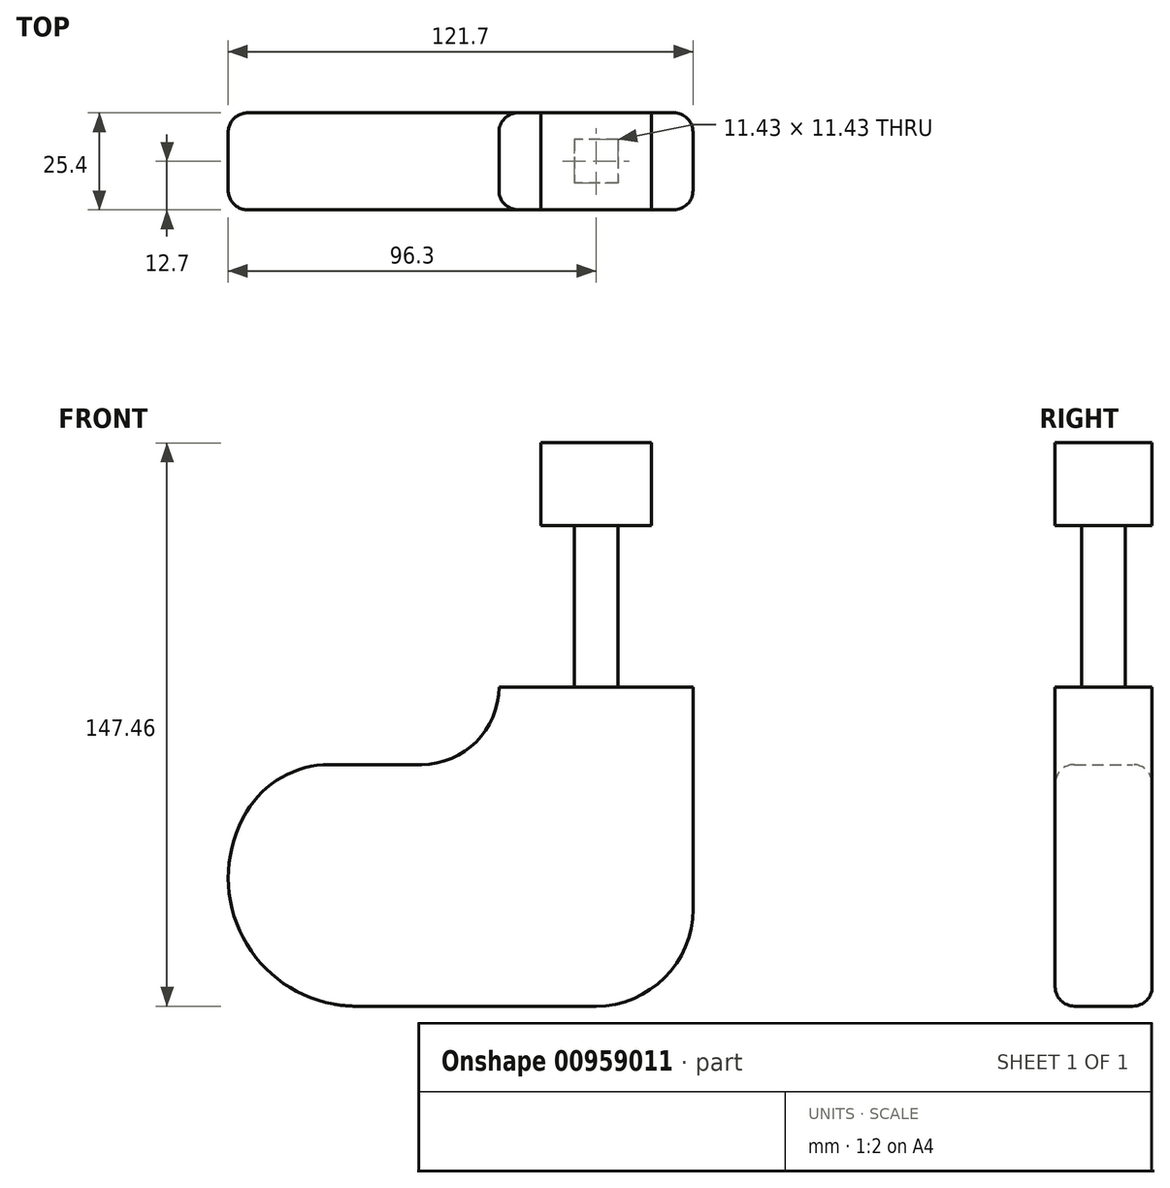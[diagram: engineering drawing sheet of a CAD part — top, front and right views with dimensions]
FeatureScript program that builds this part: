
annotation { "Feature Type Name" : "Feature", "Feature Type Description" : "" }
export const myFeature = defineFeature(function(context is Context, id is Id, definition is map)
    precondition{}
    {
        {
            var Q0;
            Q0=qCreatedBy(makeId("Front.planeOp"),FACE);
            var sketch = newSketch(context, id + "F0", { "sketchPlane" : qUnion([Q0])});
            skLineSegment(sketch, "E0.top", {"start": v(0, -63.5) * mm, "end": v(-25.4, -63.5) * mm});
            skLineSegment(sketch, "E0.left", {"start": v(25.4, 20.06) * mm, "end": v(25.4, -38.1) * mm});
            skPoint(sketch, "E0.middle", {"position": v(0, 0) * mm});
            skLineSegment(sketch, "E1.bottom", {"start": v(-25.4, -63.5) * mm, "end": v(-62.78, -63.5) * mm});
            skLineSegment(sketch, "E1.top", {"start": v(-45.72, -0.26) * mm, "end": v(-69.73, -0.26) * mm});
            skArc(sketch, "E2", {"start": v(-91.55, -12.64) * mm, "mid": v(-93.32, -43.72) * mm, "end": v(-68.83, -62.94) * mm});
            skPoint(sketch, "E3.visualSharp", {"position": v(-25.4, -0.26) * mm});
            skArc(sketch, "E3.filletArc", {"start": v(-45.72, -0.26) * mm, "mid": v(-31.35, 5.7) * mm, "end": v(-25.4, 20.06) * mm});
            skPoint(sketch, "E4.visualSharp", {"position": v(-78.6, -0.26) * mm});
            skArc(sketch, "E4.filletArc", {"start": v(-69.73, -0.26) * mm, "mid": v(-82.28, -3.57) * mm, "end": v(-91.55, -12.64) * mm});
            skPoint(sketch, "E5.visualSharp", {"position": v(-63.5, -63.5) * mm});
            skArc(sketch, "E5.filletArc", {"start": v(-68.83, -62.94) * mm, "mid": v(-65.81, -63.36) * mm, "end": v(-62.78, -63.5) * mm});
            skPoint(sketch, "E6.visualSharp", {"position": v(25.4, -63.5) * mm});
            skArc(sketch, "E6.filletArc", {"start": v(0, -63.5) * mm, "mid": v(17.96, -56.06) * mm, "end": v(25.4, -38.1) * mm});
            skLineSegment(sketch, "E7", {"start": v(-25.4, 20.06) * mm, "end": v(25.4, 20.06) * mm});
            skPoint(sketch, "E0.bottom.start.orphan", {"position": v(25.4, 63.5) * mm});
            skPoint(sketch, "E0.right.start.orphan", {"position": v(-25.4, 63.5) * mm});
            skSolve(sketch);
        }
        {
            var Q0;
            Q0 = qSketchRegion(id + "F0", true);
            extrude(context, id + "F1", {"entities" : qUnion([Q0]), "depth" : 25.4 * mm, "offsetDistance" : 25.4 * mm});
        }
        {
            var Q0;
            Q0=makeQuery(id+"F1.opExtrude","CAP_EDGE",EDGE,{"disambiguationData":[OSD([sQuery(id+"F0.wireOp",EDGE,"E2")])],"isStart":false});
            var Q1;
            Q1=makeQuery(id+"F1.opExtrude","CAP_EDGE",EDGE,{"disambiguationData":[OSD([sQuery(id+"F0.wireOp",EDGE,"E2")])],"isStart":true});
            fillet(context, id + "F2", {"entities" : qUnion([Q0, Q1]), "radius" : 5.08 * mm, "tangentPropagation" : true, "allowEdgeOverflow" : false});
        }
        {
            var Q0;
            Q0=makeQuery(id+"F1.opExtrude","SWEPT_FACE",FACE,{"disambiguationData":[OSD([sQuery(id+"F0.wireOp",EDGE,"E7")])]});
            var sketch = newSketch(context, id + "F3", { "sketchPlane" : qUnion([Q0])});
            skLineSegment(sketch, "E8.bottom", {"start": v(5.72, -6.99) * mm, "end": v(-5.72, -6.99) * mm});
            skLineSegment(sketch, "E8.top", {"start": v(5.72, -18.42) * mm, "end": v(-5.72, -18.42) * mm});
            skLineSegment(sketch, "E8.left", {"start": v(5.72, -6.99) * mm, "end": v(5.72, -18.42) * mm});
            skLineSegment(sketch, "E8.right", {"start": v(-5.72, -6.99) * mm, "end": v(-5.72, -18.42) * mm});
            skPoint(sketch, "E8.middle", {"position": v(0, -12.7) * mm});
            skPoint(sketch, "E8.middle.positionSnap0", {"position": v(25.4, -12.7) * mm});
            skPoint(sketch, "E8.centerSnap0", {"position": v(25.4, -12.7) * mm});
            skSolve(sketch);
        }
        {
            var Q0;
            Q0 = qSketchRegion(id + "F3", true);
            extrude(context, id + "F4", {"entities" : qUnion([Q0]), "operationType" : NewBodyOperationType.ADD, "depth" : 50.8 * mm, "offsetDistance" : 25.4 * mm});
        }
        {
            var Q0;
            Q0=makeQuery(id+"F1.opExtrude","CAP_FACE",FACE,{"disambiguationData":[OSD([sQuery(id+"F0.wireOp",EDGE,"E0.top"),sQuery(id+"F0.wireOp",EDGE,"E0.left"),sQuery(id+"F0.wireOp",EDGE,"E1.bottom"),sQuery(id+"F0.wireOp",EDGE,"E1.top"),sQuery(id+"F0.wireOp",EDGE,"E2"),sQuery(id+"F0.wireOp",EDGE,"E3.filletArc"),sQuery(id+"F0.wireOp",EDGE,"E4.filletArc"),sQuery(id+"F0.wireOp",EDGE,"E5.filletArc"),sQuery(id+"F0.wireOp",EDGE,"E6.filletArc"),sQuery(id+"F0.wireOp",EDGE,"E7")])],"isStart":false});
            cPlane(context, id + "F5", {"entities" : qUnion([Q0]), "cplaneType" : CPlaneType.OFFSET, "offset" : 0 * mm, "width" : 152.4 * mm, "height" : 152.4 * mm});
        }
        {
            var Q0;
            Q0=qCreatedBy(id+"F5.planeOp",FACE);
            var sketch = newSketch(context, id + "F6", { "sketchPlane" : qUnion([Q0])});
            skLineSegment(sketch, "E9.left", {"start": v(14.46, 83.96) * mm, "end": v(14.46, 71.1) * mm});
            skLineSegment(sketch, "E9.right", {"start": v(-14.46, 83.96) * mm, "end": v(-14.46, 71.1) * mm});
            skPoint(sketch, "E9.middle", {"position": v(0, 71.1) * mm});
            skPoint(sketch, "E9.top.end.orphan", {"position": v(-14.46, 45.36) * mm});
            skPoint(sketch, "E10.orphan", {"position": v(14.46, 45.36) * mm});
            skLineSegment(sketch, "E11.bottom", {"start": v(14.46, 62.36) * mm, "end": v(-14.46, 62.36) * mm});
            skLineSegment(sketch, "E11.left", {"start": v(14.46, 62.36) * mm, "end": v(14.46, 79.83) * mm});
            skLineSegment(sketch, "E11.right", {"start": v(-14.46, 62.36) * mm, "end": v(-14.46, 79.83) * mm});
            skLineSegment(sketch, "E12", {"start": v(-14.46, 83.96) * mm, "end": v(14.46, 83.96) * mm});
            skPoint(sketch, "E9.bottom.start.orphan", {"position": v(14.46, 96.83) * mm});
            skPoint(sketch, "E13.orphan", {"position": v(-14.46, 96.83) * mm});
            skSolve(sketch);
        }
        {
            var Q0;
            Q0 = qSketchRegion(id + "F6", true);
            var Q1;
            Q1=makeQuery(id+"F1.opExtrude","CAP_FACE",FACE,{"disambiguationData":[OSD([sQuery(id+"F0.wireOp",EDGE,"E0.top"),sQuery(id+"F0.wireOp",EDGE,"E0.left"),sQuery(id+"F0.wireOp",EDGE,"E1.bottom"),sQuery(id+"F0.wireOp",EDGE,"E1.top"),sQuery(id+"F0.wireOp",EDGE,"E2"),sQuery(id+"F0.wireOp",EDGE,"E3.filletArc"),sQuery(id+"F0.wireOp",EDGE,"E4.filletArc"),sQuery(id+"F0.wireOp",EDGE,"E5.filletArc"),sQuery(id+"F0.wireOp",EDGE,"E6.filletArc"),sQuery(id+"F0.wireOp",EDGE,"E7")])],"isStart":true});
            extrude(context, id + "F7", {"entities" : qUnion([Q0]), "operationType" : NewBodyOperationType.ADD, "endBound" : BoundingType.UP_TO_SURFACE, "oppositeDirection" : true, "depth" : 25.4 * mm, "endBoundEntityFace" : qUnion([Q1]), "offsetDistance" : 25.4 * mm});
        }
    });
